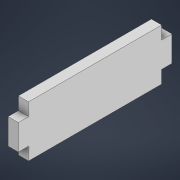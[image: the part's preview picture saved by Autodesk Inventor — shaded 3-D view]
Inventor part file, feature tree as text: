
AUTODESK INVENTOR PART (.ipt)
format: ipt  version: 2022 (Build 260153000, 153)  size: 97,792 bytes
history: native  units: mm
features: other x1, extrude x1, sketch x1
ambient origin geometry x8: Origin, YZ Plane, XZ Plane, XY Plane, X Axis, Y Axis, Z Axis, Center Point
bodies: Body1 (feature_tree)
feature tree (3):
  other  "Твердое тело1"
  extrude  "Выдавливание1"  Depth=20.0mm
  sketch  "Эскиз1"
